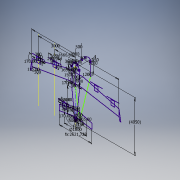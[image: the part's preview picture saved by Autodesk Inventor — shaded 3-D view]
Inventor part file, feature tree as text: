
AUTODESK INVENTOR PART (.ipt)
format: ipt  version: 2017 (Build 210142000, 142)  size: 153,088 bytes
history: native  units: mm
features: other x4, plane x2
ambient origin geometry x8: Origin, YZ Plane, XZ Plane, XY Plane, X Axis, Y Axis, Z Axis, Center Point
feature tree (6):
  other  "Top"
  other  "Work Axis1"
  other  "Work Axis2"
  other  "Work Axis3"
  plane  "Work Plane1"
  plane  "Work Plane2"
